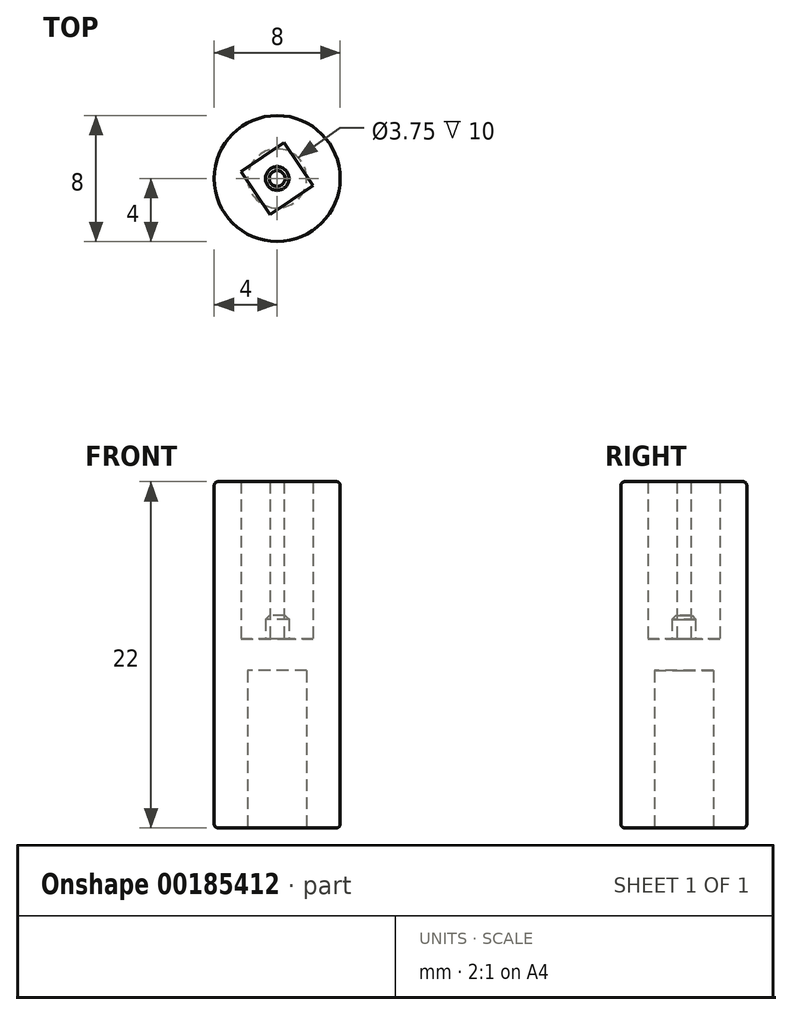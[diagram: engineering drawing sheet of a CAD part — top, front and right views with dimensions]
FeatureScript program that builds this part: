
annotation { "Feature Type Name" : "Feature", "Feature Type Description" : "" }
export const myFeature = defineFeature(function(context is Context, id is Id, definition is map)
    precondition{}
    {
        {
            var Q0;
            Q0=qCreatedBy(makeId("Top.planeOp"),FACE);
            var sketch = newSketch(context, id + "F0", { "sketchPlane" : qUnion([Q0])});
            skCircle(sketch, "E0", {"center": v(0, 0) * mm, "radius": 4 * mm});
            skCircle(sketch, "E1", {"center": v(0, 0) * mm, "radius": 1.88 * mm});
            skSolve(sketch);
        }
        {
            var Q0;
            Q0 = qSketchRegion(id + "F0", true);
            extrude(context, id + "F1", {"entities" : qUnion([Q0]), "depth" : 10 * mm});
        }
        {
            var Q0;
            Q0=makeQuery(id+"F1.opExtrude","CAP_FACE",FACE,{"disambiguationData":[OSD([sQuery(id+"F0.wireOp",EDGE,"E0"),sQuery(id+"F0.wireOp",EDGE,"E1")])],"isStart":false});
            var sketch = newSketch(context, id + "F2", { "sketchPlane" : qUnion([Q0])});
            skCircle(sketch, "E2", {"center": v(0, 0) * mm, "radius": 4 * mm});
            skSolve(sketch);
        }
        {
            var Q0;
            Q0 = qSketchRegion(id + "F2", true);
            extrude(context, id + "F3", {"entities" : qUnion([Q0]), "operationType" : NewBodyOperationType.ADD, "depth" : 2 * mm});
        }
        {
            var Q0;
            Q0=makeQuery(id+"F3.opExtrude","CAP_FACE",FACE,{"disambiguationData":[OSD([sQuery(id+"F2.wireOp",EDGE,"E2")])],"isStart":false});
            var sketch = newSketch(context, id + "F4", { "sketchPlane" : qUnion([Q0])});
            skCircle(sketch, "E3", {"center": v(0, 0) * mm, "radius": 0.75 * mm});
            skSolve(sketch);
        }
        {
            var Q0;
            Q0=makeQuery(id+"F4.imprint","IMPRINT",FACE,{"disambiguationData":[TD([[makeQuery(id+"F4.imprint","IMPRINT",EDGE,{"derivedFrom":sQuery(id+"F4.wireOp",EDGE,"E3")}),1.0]])]});
            extrude(context, id + "F5", {"entities" : qUnion([Q0]), "operationType" : NewBodyOperationType.ADD, "depth" : 1.5 * mm});
        }
        {
            var Q0;
            Q0=makeQuery(id+"F5.opExtrude","CAP_EDGE",EDGE,{"disambiguationData":[OSD([sQuery(id+"F4.wireOp",EDGE,"E3")])],"isStart":false});
            chamfer(context, id + "F6", {"entities" : qUnion([Q0]), "width" : .25 * mm, "tangentPropagation" : true});
        }
        {
            var Q0;
            Q0=makeQuery(id+"F3.opExtrude","CAP_FACE",FACE,{"disambiguationData":[OSD([sQuery(id+"F2.wireOp",EDGE,"E2")])],"isStart":false});
            var sketch = newSketch(context, id + "F7", { "sketchPlane" : qUnion([Q0])});
            skCircle(sketch, "E4", {"center": v(0, 0) * mm, "radius": 4 * mm});
            skCircle(sketch, "E5.cCircle", {"center": v(0, 0) * mm, "radius": 2.33 * mm, "construction": true});
            skLineSegment(sketch, "E5.0", {"start": v(-2.3, 0.45) * mm, "end": v(0.45, 2.3) * mm});
            skLineSegment(sketch, "E5.1", {"start": v(0.45, 2.3) * mm, "end": v(2.3, -0.45) * mm});
            skLineSegment(sketch, "E5.2", {"start": v(2.3, -0.45) * mm, "end": v(-0.45, -2.3) * mm});
            skLineSegment(sketch, "E5.3", {"start": v(-0.45, -2.3) * mm, "end": v(-2.3, 0.45) * mm});
            skSolve(sketch);
        }
        {
            var Q0;
            Q0=makeQuery(id+"F7.imprint","IMPRINT",FACE,{"disambiguationData":[TD([[makeQuery(id+"F7.imprint","IMPRINT",EDGE,{"derivedFrom":sQuery(id+"F7.wireOp",EDGE,"E4")}),1.0]])]});
            extrude(context, id + "F8", {"entities" : qUnion([Q0]), "operationType" : NewBodyOperationType.ADD, "depth" : 10 * mm});
        }
        {
            var Q0;
            Q0=makeQuery(id+"F8.opExtrude","CAP_EDGE",EDGE,{"disambiguationData":[OSD([sQuery(id+"F7.wireOp",EDGE,"E4")])],"isStart":false});
            fillet(context, id + "F9", {"entities" : qUnion([Q0]), "radius" : .25 * mm, "tangentPropagation" : true, "allowEdgeOverflow" : false});
        }
        {
            var Q0;
            Q0=makeQuery(id+"F1.opExtrude","CAP_EDGE",EDGE,{"disambiguationData":[OSD([sQuery(id+"F0.wireOp",EDGE,"E0")])],"isStart":true});
            fillet(context, id + "F10", {"entities" : qUnion([Q0]), "radius" : .25 * mm, "tangentPropagation" : true, "allowEdgeOverflow" : false});
        }
    });
